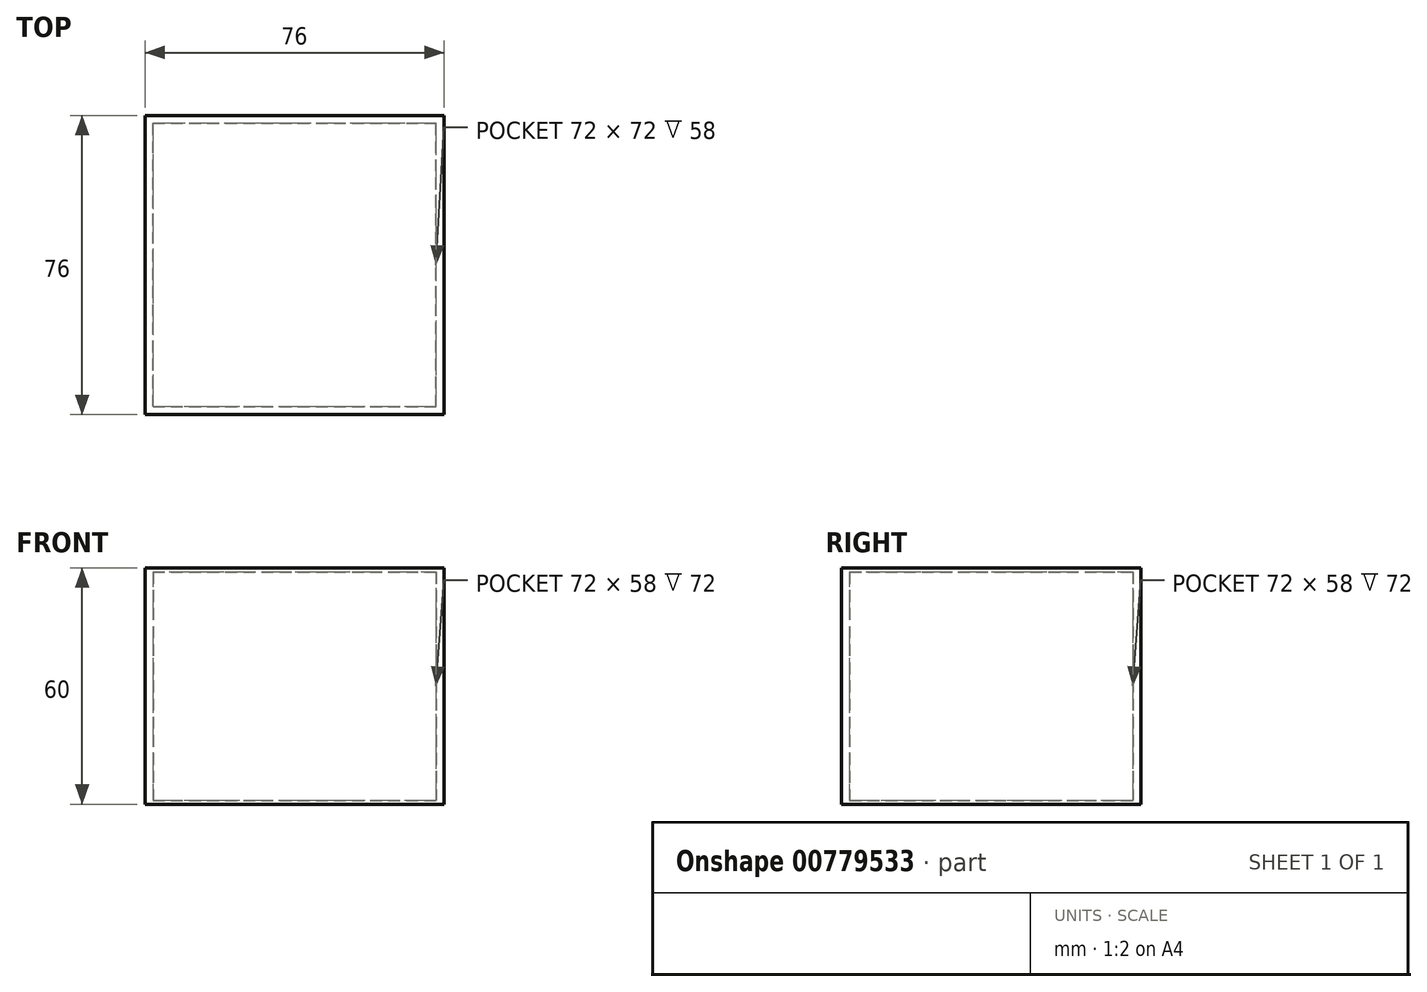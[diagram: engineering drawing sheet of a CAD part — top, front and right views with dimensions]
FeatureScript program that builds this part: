
annotation { "Feature Type Name" : "Feature", "Feature Type Description" : "" }
export const myFeature = defineFeature(function(context is Context, id is Id, definition is map)
    precondition{}
    {
        {
            var Q0;
            Q0=qCreatedBy(makeId("Top.planeOp"),FACE);
            var sketch = newSketch(context, id + "F0", { "sketchPlane" : qUnion([Q0])});
            skLineSegment(sketch, "E0.bottom", {"start": v(-37, -37) * mm, "end": v(37, -37) * mm});
            skLineSegment(sketch, "E0.top", {"start": v(-37, 37) * mm, "end": v(37, 37) * mm});
            skLineSegment(sketch, "E0.left", {"start": v(-37, -37) * mm, "end": v(-37, 37) * mm});
            skLineSegment(sketch, "E0.right", {"start": v(37, -37) * mm, "end": v(37, 37) * mm});
            skPoint(sketch, "E0.middle", {"position": v(0, 0) * mm});
            skSolve(sketch);
        }
        {
            var Q0;
            Q0=makeQuery(id+"F0.imprint","IMPRINT",FACE,{"disambiguationData":[TD([[makeQuery(id+"F0.imprint","IMPRINT",EDGE,{"derivedFrom":sQuery(id+"F0.wireOp",EDGE,"E0.bottom")}),1.0]])]});
            extrude(context, id + "F1", {"entities" : qUnion([Q0]), "depth" : 59 * mm, "offsetDistance" : 25.4 * mm});
        }
        {
            var Q0;
            Q0=makeQuery(id+"F1.opExtrude","CAP_FACE",FACE,{"disambiguationData":[OSD([sQuery(id+"F0.wireOp",EDGE,"E0.bottom"),sQuery(id+"F0.wireOp",EDGE,"E0.top"),sQuery(id+"F0.wireOp",EDGE,"E0.left"),sQuery(id+"F0.wireOp",EDGE,"E0.right")])],"isStart":false});
            shell(context, id + "F2", {"entities" : qUnion([Q0]), "thickness" : 1 * mm});
        }
        {
            var Q0;
            Q0=qCreatedBy(makeId("Top.planeOp"),FACE);
            var sketch = newSketch(context, id + "F3", { "sketchPlane" : qUnion([Q0])});
            skLineSegment(sketch, "E1.bottom", {"start": v(-37, -37) * mm, "end": v(37, -37) * mm});
            skLineSegment(sketch, "E1.top", {"start": v(-37, 37) * mm, "end": v(37, 37) * mm});
            skLineSegment(sketch, "E1.left", {"start": v(-37, -37) * mm, "end": v(-37, 37) * mm});
            skLineSegment(sketch, "E1.right", {"start": v(37, -37) * mm, "end": v(37, 37) * mm});
            skPoint(sketch, "E1.middle", {"position": v(0, 0) * mm});
            skLineSegment(sketch, "E2.0", {"start": v(-38, -38) * mm, "end": v(38, -38) * mm});
            skLineSegment(sketch, "E2.1", {"start": v(-38, -38) * mm, "end": v(-38, 38) * mm});
            skLineSegment(sketch, "E2.2", {"start": v(-38, 38) * mm, "end": v(38, 38) * mm});
            skLineSegment(sketch, "E2.3", {"start": v(38, -38) * mm, "end": v(38, 38) * mm});
            skSolve(sketch);
        }
        {
            var Q0;
            Q0 = qSketchRegion(id + "F3", true);
            var Q1;
            Q1=makeQuery(id+"F1.opExtrude","CAP_FACE",FACE,{"disambiguationData":[OSD([sQuery(id+"F0.wireOp",EDGE,"E0.bottom"),sQuery(id+"F0.wireOp",EDGE,"E0.top"),sQuery(id+"F0.wireOp",EDGE,"E0.left"),sQuery(id+"F0.wireOp",EDGE,"E0.right")])],"isStart":false});
            extrude(context, id + "F4", {"entities" : qUnion([Q0]), "operationType" : NewBodyOperationType.ADD, "depth" : 60 * mm, "endBoundEntityFace" : qUnion([Q1]), "offsetDistance" : 25.4 * mm});
        }
        {
            var Q0;
            Q0=makeQuery(id+"F4.opExtrude","SWEPT_FACE",FACE,{"disambiguationData":[OSD([sQuery(id+"F3.wireOp",EDGE,"E1.left")])]});
            var sketch = newSketch(context, id + "F5", { "sketchPlane" : qUnion([Q0])});
            skLineSegment(sketch, "E3.bottom", {"start": v(37, 60) * mm, "end": v(-37, 60) * mm});
            skLineSegment(sketch, "E3.top", {"start": v(37, 59) * mm, "end": v(-37, 59) * mm});
            skLineSegment(sketch, "E3.left", {"start": v(37, 60) * mm, "end": v(37, 59) * mm});
            skLineSegment(sketch, "E3.right", {"start": v(-37, 60) * mm, "end": v(-37, 59) * mm});
            skSolve(sketch);
        }
        {
            var Q0;
            Q0=makeQuery(id+"F5.imprint","IMPRINT",FACE,{"disambiguationData":[TD([[makeQuery(id+"F5.imprint","IMPRINT",EDGE,{"derivedFrom":sQuery(id+"F5.wireOp",EDGE,"E3.bottom")}),-1.0]])]});
            var Q1;
            Q1=makeQuery(id+"F4.opExtrude","SWEPT_FACE",FACE,{"disambiguationData":[OSD([sQuery(id+"F3.wireOp",EDGE,"E1.right")])]});
            extrude(context, id + "F6", {"entities" : qUnion([Q0]), "operationType" : NewBodyOperationType.ADD, "endBound" : BoundingType.UP_TO_SURFACE, "depth" : 25.4 * mm, "endBoundEntityFace" : qUnion([Q1]), "offsetDistance" : 25.4 * mm});
        }
    });
